# Revit family: EF_Veti-4x4-3-Two-Pin-No-Switching-1-Three-Pin-with-Switching-Power-Point
name_source: partatom
category: Electrical Fixtures
revit_build: Autodesk Revit 2016 (Build: 20150220_1215(x64)
units: mm (PartAtom-declared; Revit-internal decimal feet)

## family parameters
Always vertical = Yes
Cut with Voids When Loaded = No
Maintain Annotation Orientation = No
Part Type = Normal
Room Calculation Point = No
Round Connector Dimension = Use Diameter
Shared = No
Work Plane-Based = No

## types (2) — shared parameters
Amperage = 16 A
Description = 4x4 3 Two Pin No Switching -1 Three Pin with Switching Power Point
Load = 2860 VA
Manufacturer = VETI
Switch Voltage = 220 V
Type Comments = Plug Points
URL = http://www.major-tech.com
Voltage_x = 220 V

## per-type parameters (varying)
| type | Made by | URL for TCP |
| 3 Two Pin No Switching |  |  |
| Two Pin No Switching 1 Three Pin with Switching Power Point | Tolani Civil Projects cc | http://www.tcpbim.co.za |

## geometry (parser evidence)
native form markers: Sweep x9
no freeform markers — native parametric forms only
